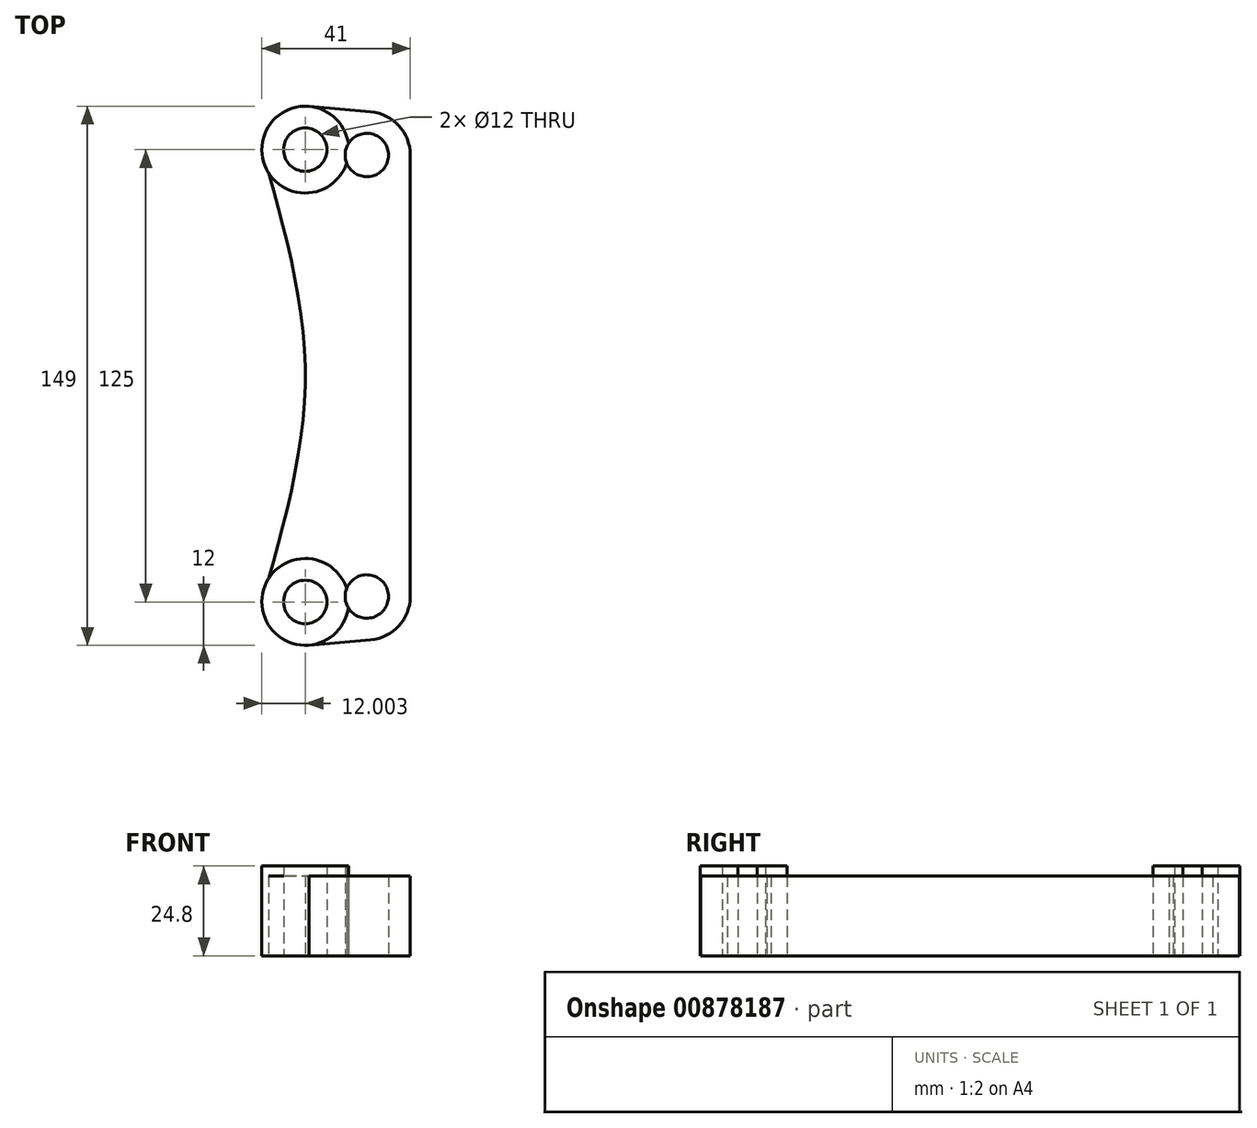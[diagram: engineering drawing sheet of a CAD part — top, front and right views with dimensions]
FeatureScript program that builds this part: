
annotation { "Feature Type Name" : "Feature", "Feature Type Description" : "" }
export const myFeature = defineFeature(function(context is Context, id is Id, definition is map)
    precondition{}
    {
        {
            var Q0;
            Q0=qCreatedBy(makeId("Top.planeOp"),FACE);
            var sketch = newSketch(context, id + "F0", { "sketchPlane" : qUnion([Q0])});
            skCircle(sketch, "E0", {"center": v(0, 0) * mm, "radius": 151 * mm, "construction": true});
            skCircle(sketch, "E1", {"center": v(0, 0) * mm, "radius": 70 * mm, "construction": true});
            skLineSegment(sketch, "E2", {"start": v(-151, 0) * mm, "end": v(-105, 0) * mm});
            skLineSegment(sketch, "E3", {"start": v(-105, 0) * mm, "end": v(-70, 0) * mm});
            skCircle(sketch, "E4", {"center": v(0, 0) * mm, "radius": 165 * mm, "construction": true});
            skCircle(sketch, "E5", {"center": v(-34.34, 61) * mm, "radius": 6 * mm});
            skCircle(sketch, "E6", {"center": v(-34.34, -61) * mm, "radius": 6 * mm});
            skLineSegment(sketch, "E7", {"start": v(-34.34, 61) * mm, "end": v(-34.34, -61) * mm, "construction": true});
            skCircle(sketch, "E8", {"center": v(-51.34, 62.5) * mm, "radius": 6 * mm});
            skCircle(sketch, "E9", {"center": v(-51.34, -62.5) * mm, "radius": 6 * mm});
            skLineSegment(sketch, "E10", {"start": v(-34.34, 61) * mm, "end": v(-51.34, 61) * mm, "construction": true});
            skLineSegment(sketch, "E11", {"start": v(-51.34, 62.5) * mm, "end": v(-51.34, 0) * mm, "construction": true});
            skLineSegment(sketch, "E12", {"start": v(-51.34, 0) * mm, "end": v(-51.34, -62.5) * mm, "construction": true});
            skCircle(sketch, "E13", {"center": v(-34.34, -61) * mm, "radius": 12 * mm});
            skCircle(sketch, "E14", {"center": v(-51.34, -62.5) * mm, "radius": 12 * mm});
            skCircle(sketch, "E15", {"center": v(-34.34, 61) * mm, "radius": 12 * mm});
            skCircle(sketch, "E16", {"center": v(-51.34, 62.5) * mm, "radius": 12 * mm});
            skLineSegment(sketch, "E17", {"start": v(-51.34, -62.5) * mm, "end": v(-63.34, -62.5) * mm});
            skLineSegment(sketch, "E18", {"start": v(-34.34, -61) * mm, "end": v(-22.34, -61) * mm});
            skLineSegment(sketch, "E19", {"start": v(-34.34, 61) * mm, "end": v(-22.34, 61) * mm, "construction": true});
            skLineSegment(sketch, "E20", {"start": v(-33.28, 72.95) * mm, "end": v(-50.28, 74.45) * mm});
            skLineSegment(sketch, "E21", {"start": v(-50.28, -74.45) * mm, "end": v(-33.28, -72.95) * mm});
            skLineSegment(sketch, "E22", {"start": v(-51.34, 62.5) * mm, "end": v(-63.34, 62.5) * mm});
            skLineSegment(sketch, "E23", {"start": v(-22.34, 61) * mm, "end": v(-22.34, -61) * mm});
            skFitSpline(sketch, "E24", {"points": [v(-63.34, 62.5) * mm, v(-51.34, 0) * mm, v(-63.34, -62.5) * mm], "startDerivative": vector(36, -125) * mm, "endDerivative": vector(-36, -125) * mm});
            skSolve(sketch);
        }
        {
            var Q0;
            {var subQ2=sQuery(id+"F0.wireOp",EDGE,"E22");var subQ6=sQuery(id+"F0.wireOp",EDGE,"E8");var subQ8=makeQuery(id+"F0.imprint","INTERSECT",VERTEX,{"derivedFrom":[subQ6,subQ2]});Q0=makeQuery(id+"F0.imprint","IMPRINT",FACE,{"disambiguationData":[TD([[makeQuery(id+"F0.imprint","IMPRINT",EDGE,{"disambiguationData":[TD([[subQ8,1.0]])],"derivedFrom":subQ6}),-1.0]])]});}
            var Q1;
            {var subQ5=sQuery(id+"F0.wireOp",EDGE,"E8");var subQ7=sQuery(id+"F0.wireOp",EDGE,"E22");var subQ8=makeQuery(id+"F0.imprint","INTERSECT",VERTEX,{"derivedFrom":[subQ5,subQ7]});Q1=makeQuery(id+"F0.imprint","IMPRINT",FACE,{"disambiguationData":[TD([[makeQuery(id+"F0.imprint","IMPRINT",EDGE,{"disambiguationData":[TD([[subQ8,-1.0]])],"derivedFrom":subQ5}),-1.0]])]});}
            var Q2;
            {var subQ3=sQuery(id+"F0.wireOp",EDGE,"E16");var subQ7=sQuery(id+"F0.wireOp",EDGE,"E5");var subQ8=makeQuery(id+"F0.imprint","INTERSECT",VERTEX,{"disambiguationData":[OD(0.0)],"derivedFrom":[subQ7,subQ3]});Q2=makeQuery(id+"F0.imprint","IMPRINT",FACE,{"disambiguationData":[TD([[makeQuery(id+"F0.imprint","IMPRINT",EDGE,{"disambiguationData":[TD([[subQ8,-1.0]])],"derivedFrom":subQ7}),-1.0]])]});}
            var Q3;
            {var subQ0=sQuery(id+"F0.wireOp",EDGE,"E24");var subQ1=sQuery(id+"F0.wireOp",EDGE,"E16");var subQ3=makeQuery(id+"F0.imprint","INTERSECT",VERTEX,{"derivedFrom":[subQ1,subQ0]});Q3=makeQuery(id+"F0.imprint","IMPRINT",FACE,{"disambiguationData":[TD([[makeQuery(id+"F0.imprint","IMPRINT",EDGE,{"disambiguationData":[TD([[subQ3,1.0]])],"derivedFrom":subQ1}),1.0]])]});}
            var Q4;
            {var subQ1=sQuery(id+"F0.wireOp",EDGE,"E17");var subQ4=sQuery(id+"F0.wireOp",EDGE,"E9");var subQ5=makeQuery(id+"F0.imprint","INTERSECT",VERTEX,{"derivedFrom":[subQ4,subQ1]});Q4=makeQuery(id+"F0.imprint","IMPRINT",FACE,{"disambiguationData":[TD([[makeQuery(id+"F0.imprint","IMPRINT",EDGE,{"disambiguationData":[TD([[subQ5,1.0]])],"derivedFrom":subQ4}),-1.0]])]});}
            var Q5;
            {var subQ0=sQuery(id+"F0.wireOp",EDGE,"E24");var subQ1=sQuery(id+"F0.wireOp",EDGE,"E14");var subQ3=makeQuery(id+"F0.imprint","INTERSECT",VERTEX,{"derivedFrom":[subQ1,subQ0]});Q5=makeQuery(id+"F0.imprint","IMPRINT",FACE,{"disambiguationData":[TD([[makeQuery(id+"F0.imprint","IMPRINT",EDGE,{"disambiguationData":[TD([[subQ3,-1.0]])],"derivedFrom":subQ1}),1.0]])]});}
            var Q6;
            {var subQ4=sQuery(id+"F0.wireOp",EDGE,"E17");var subQ6=sQuery(id+"F0.wireOp",EDGE,"E9");var subQ7=makeQuery(id+"F0.imprint","INTERSECT",VERTEX,{"derivedFrom":[subQ6,subQ4]});Q6=makeQuery(id+"F0.imprint","IMPRINT",FACE,{"disambiguationData":[TD([[makeQuery(id+"F0.imprint","IMPRINT",EDGE,{"disambiguationData":[TD([[subQ7,-1.0]])],"derivedFrom":subQ6}),-1.0]])]});}
            var Q7;
            {var subQ3=sQuery(id+"F0.wireOp",EDGE,"E14");var subQ5=sQuery(id+"F0.wireOp",EDGE,"E6");var subQ6=makeQuery(id+"F0.imprint","INTERSECT",VERTEX,{"disambiguationData":[OD(0.0)],"derivedFrom":[subQ5,subQ3]});Q7=makeQuery(id+"F0.imprint","IMPRINT",FACE,{"disambiguationData":[TD([[makeQuery(id+"F0.imprint","IMPRINT",EDGE,{"disambiguationData":[TD([[subQ6,-1.0]])],"derivedFrom":subQ5}),-1.0]])]});}
            extrude(context, id + "F1", {"entities" : qUnion([Q0, Q1, Q2, Q3, Q4, Q5, Q6, Q7]), "depth" : 24.8 * mm, "offsetDistance" : 25 * mm});
        }
        {
            var Q0;
            {var subQ5=sQuery(id+"F0.wireOp",EDGE,"E23");Q0=makeQuery(id+"F0.imprint","IMPRINT",FACE,{"disambiguationData":[TD([[makeQuery(id+"F0.imprint","IMPRINT",EDGE,{"derivedFrom":subQ5}),-1.0]])]});}
            var Q1;
            {var subQ0=sQuery(id+"F0.wireOp",EDGE,"E18");var subQ1=sQuery(id+"F0.wireOp",EDGE,"E6");var subQ2=makeQuery(id+"F0.imprint","INTERSECT",VERTEX,{"derivedFrom":[subQ1,subQ0]});Q1=makeQuery(id+"F0.imprint","IMPRINT",FACE,{"disambiguationData":[TD([[makeQuery(id+"F0.imprint","IMPRINT",EDGE,{"disambiguationData":[TD([[subQ2,-1.0]])],"derivedFrom":subQ1}),-1.0]])]});}
            var Q2;
            {var subQ1=sQuery(id+"F0.wireOp",EDGE,"E6");var subQ5=sQuery(id+"F0.wireOp",EDGE,"E18");var subQ8=makeQuery(id+"F0.imprint","INTERSECT",VERTEX,{"derivedFrom":[subQ1,subQ5]});Q2=makeQuery(id+"F0.imprint","IMPRINT",FACE,{"disambiguationData":[TD([[makeQuery(id+"F0.imprint","IMPRINT",EDGE,{"disambiguationData":[TD([[subQ8,1.0]])],"derivedFrom":subQ1}),-1.0]])]});}
            var Q3;
            {var subQ2=sQuery(id+"F0.wireOp",EDGE,"E16");var subQ6=sQuery(id+"F0.wireOp",EDGE,"E5");var subQ8=makeQuery(id+"F0.imprint","INTERSECT",VERTEX,{"disambiguationData":[OD(0.0)],"derivedFrom":[subQ6,subQ2]});Q3=makeQuery(id+"F0.imprint","IMPRINT",FACE,{"disambiguationData":[TD([[makeQuery(id+"F0.imprint","IMPRINT",EDGE,{"disambiguationData":[TD([[subQ8,1.0]])],"derivedFrom":subQ6}),-1.0]])]});}
            var Q4;
            {var subQ0=sQuery(id+"F0.wireOp",EDGE,"E21");Q4=makeQuery(id+"F0.imprint","IMPRINT",FACE,{"disambiguationData":[TD([[makeQuery(id+"F0.imprint","IMPRINT",EDGE,{"derivedFrom":subQ0}),1.0]])]});}
            var Q5;
            {var subQ0=sQuery(id+"F0.wireOp",EDGE,"E20");Q5=makeQuery(id+"F0.imprint","IMPRINT",FACE,{"disambiguationData":[TD([[makeQuery(id+"F0.imprint","IMPRINT",EDGE,{"derivedFrom":subQ0}),1.0]])]});}
            extrude(context, id + "F2", {"entities" : qUnion([Q0, Q1, Q2, Q3, Q4, Q5]), "depth" : 22 * mm, "offsetDistance" : 25 * mm});
        }
    });
